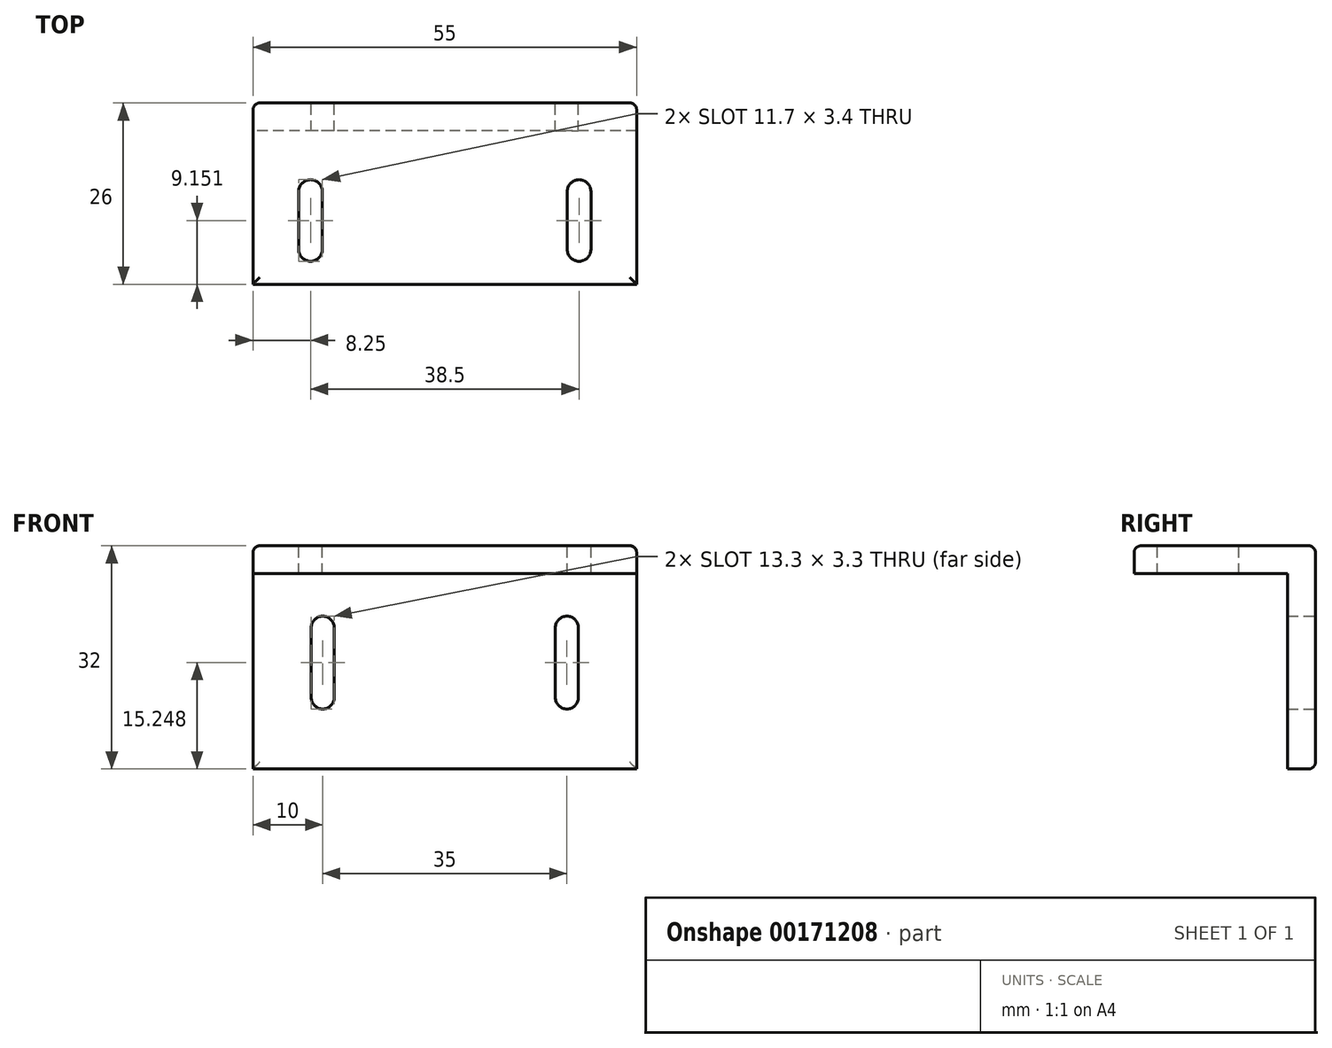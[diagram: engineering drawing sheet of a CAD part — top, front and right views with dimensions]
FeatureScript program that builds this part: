
annotation { "Feature Type Name" : "Feature", "Feature Type Description" : "" }
export const myFeature = defineFeature(function(context is Context, id is Id, definition is map)
    precondition{}
    {
        {
            var Q0;
            Q0=qCreatedBy(makeId("Right.planeOp"),FACE);
            var sketch = newSketch(context, id + "F0", { "sketchPlane" : qUnion([Q0])});
            skLineSegment(sketch, "E0.bottom", {"start": v(0, 0) * mm, "end": v(-26, 0) * mm});
            skLineSegment(sketch, "E0.top", {"start": v(0, -32) * mm, "end": v(-4, -32) * mm});
            skLineSegment(sketch, "E0.left", {"start": v(0, 0) * mm, "end": v(0, -32) * mm});
            skLineSegment(sketch, "E0.right", {"start": v(-26, 0) * mm, "end": v(-26, -4) * mm});
            skLineSegment(sketch, "E1.top", {"start": v(-26, -4) * mm, "end": v(-4, -4) * mm});
            skLineSegment(sketch, "E1.right", {"start": v(-4, -32) * mm, "end": v(-4, -4) * mm});
            skSolve(sketch);
        }
        {
            var Q0;
            Q0=makeQuery(id+"F0.imprint","IMPRINT",FACE,{"disambiguationData":[TD([[makeQuery(id+"F0.imprint","IMPRINT",EDGE,{"derivedFrom":sQuery(id+"F0.wireOp",EDGE,"E0.bottom")}),1.0]])]});
            extrude(context, id + "F1", {"entities" : qUnion([Q0]), "endBound" : BoundingType.SYMMETRIC, "depth" : 55 * mm});
        }
        {
            var Q0;
            Q0=qCreatedBy(makeId("Top.planeOp"),FACE);
            var sketch = newSketch(context, id + "F2", { "sketchPlane" : qUnion([Q0])});
            skArc(sketch, "E2", {"start": v(-20.95, -21) * mm, "mid": v(-19.25, -22.7) * mm, "end": v(-17.55, -21) * mm});
            skLineSegment(sketch, "E3.bottom", {"start": v(-17.55, -12.7) * mm, "end": v(-17.55, -12.7) * mm});
            skLineSegment(sketch, "E3.top", {"start": v(-19.25, -21) * mm, "end": v(-19.25, -21) * mm});
            skLineSegment(sketch, "E4.bottom", {"start": v(-20.95, -21) * mm, "end": v(-17.55, -21) * mm});
            skLineSegment(sketch, "E4.right", {"start": v(-17.55, -21) * mm, "end": v(-17.55, -12.7) * mm});
            skArc(sketch, "E5", {"start": v(-17.55, -12.7) * mm, "mid": v(-19.25, -11) * mm, "end": v(-20.95, -12.7) * mm});
            skLineSegment(sketch, "E6", {"start": v(-20.95, -21) * mm, "end": v(-20.95, -12.7) * mm});
            skLineSegment(sketch, "E7.MirrorCS", {"start": v(19.25, -21) * mm, "end": v(19.25, -21) * mm});
            skLineSegment(sketch, "E8.MirrorCS", {"start": v(20.95, -21) * mm, "end": v(17.55, -21) * mm});
            skArc(sketch, "E9.MirrorCS", {"start": v(17.55, -12.7) * mm, "mid": v(19.25, -11) * mm, "end": v(20.95, -12.7) * mm});
            skArc(sketch, "E10.MirrorCS", {"start": v(20.95, -21) * mm, "mid": v(19.25, -22.7) * mm, "end": v(17.55, -21) * mm});
            skLineSegment(sketch, "E11.MirrorCS", {"start": v(17.55, -12.7) * mm, "end": v(17.55, -12.7) * mm});
            skLineSegment(sketch, "E12.MirrorCS", {"start": v(20.95, -21) * mm, "end": v(20.95, -12.7) * mm});
            skLineSegment(sketch, "E13.MirrorCS", {"start": v(17.55, -21) * mm, "end": v(17.55, -12.7) * mm});
            skSolve(sketch);
        }
        {
            var Q0;
            Q0=qSketchRegion(id+"F2",true);
            extrude(context, id + "F3", {"entities" : qUnion([Q0]), "operationType" : NewBodyOperationType.REMOVE, "endBound" : BoundingType.THROUGH_ALL, "oppositeDirection" : true, "depth" : 10 * mm});
        }
        {
            var Q0;
            Q0=makeQuery(id+"F1.opExtrude","SWEPT_EDGE",EDGE,{"disambiguationData":[OSD([sQuery(id+"F0.wireOp",EDGE,"E0.top"),sQuery(id+"F0.wireOp",EDGE,"E0.left")])]});
            var Q1;
            Q1=makeQuery(id+"F1.opExtrude","CAP_EDGE",EDGE,{"disambiguationData":[OSD([sQuery(id+"F0.wireOp",EDGE,"E0.left")])],"isStart":true});
            var Q2;
            Q2=makeQuery(id+"F1.opExtrude","CAP_EDGE",EDGE,{"disambiguationData":[OSD([sQuery(id+"F0.wireOp",EDGE,"E0.left")])],"isStart":false});
            var Q3;
            Q3=makeQuery(id+"F1.opExtrude","SWEPT_EDGE",EDGE,{"disambiguationData":[OSD([sQuery(id+"F0.wireOp",EDGE,"E0.bottom"),sQuery(id+"F0.wireOp",EDGE,"E0.left")])]});
            var Q4;
            {var subQ0=sQuery(id+"F0.wireOp",EDGE,"E0.bottom");var subQ1=sQuery(id+"F0.wireOp",EDGE,"E0.right");Q4=makeQuery(id+"F3.boolean.opBoolean","SPLIT",EDGE,{"disambiguationData":[TD([makeQuery(id+"F3.opExtrude","SWEPT_FACE",FACE,{"disambiguationData":[OSD([sQuery(id+"F2.wireOp",EDGE,"orV0qqHB-hAtN-c7Y2-ubxL-00y3ppTQjBUW.left")])]})])],"derivedFrom":makeQuery(id+"F1.opExtrude","SWEPT_EDGE",EDGE,{"disambiguationData":[OSD([subQ0,subQ1])]})});}
            var Q5;
            {var subQ0=sQuery(id+"F0.wireOp",EDGE,"E0.bottom");var subQ1=sQuery(id+"F0.wireOp",EDGE,"E0.right");Q5=makeQuery(id+"F3.boolean.opBoolean","SPLIT",EDGE,{"disambiguationData":[TD([makeQuery(id+"F3.opExtrude","SWEPT_FACE",FACE,{"disambiguationData":[OSD([sQuery(id+"F2.wireOp",EDGE,"f2039e86-be7c-4192-a979-50250873df190.MirrorCS")])]})])],"derivedFrom":makeQuery(id+"F1.opExtrude","SWEPT_EDGE",EDGE,{"disambiguationData":[OSD([subQ0,subQ1])]})});}
            var Q6;
            Q6=makeQuery(id+"F1.opExtrude","CAP_EDGE",EDGE,{"disambiguationData":[OSD([sQuery(id+"F0.wireOp",EDGE,"E0.bottom")])],"isStart":true});
            var Q7;
            Q7=makeQuery(id+"F3.boolean.opBoolean","COPY",EDGE,{"derivedFrom":makeQuery(id+"F3.opExtrude","CAP_EDGE",EDGE,{"disambiguationData":[OSD([sQuery(id+"F2.wireOp",EDGE,"40ea4abb-f649-4232-bc7a-a4a23449ed800.MirrorCS")])],"isStart":true})});
            var Q8;
            Q8=makeQuery(id+"F1.opExtrude","CAP_EDGE",EDGE,{"disambiguationData":[OSD([sQuery(id+"F0.wireOp",EDGE,"E0.bottom")])],"isStart":false});
            var Q9;
            Q9=makeQuery(id+"F3.boolean.opBoolean","COPY",EDGE,{"derivedFrom":makeQuery(id+"F3.opExtrude","CAP_EDGE",EDGE,{"disambiguationData":[OSD([sQuery(id+"F2.wireOp",EDGE,"orV0qqHB-hAtN-c7Y2-ubxL-00y3ppTQjBUW.left")])],"isStart":true})});
            var Q10;
            Q10=makeQuery(id+"F3.boolean.opBoolean","COPY",EDGE,{"derivedFrom":makeQuery(id+"F3.opExtrude","CAP_EDGE",EDGE,{"disambiguationData":[OSD([sQuery(id+"F2.wireOp",EDGE,"f2039e86-be7c-4192-a979-50250873df190.MirrorCS")])],"isStart":true})});
            fillet(context, id + "F4", {"entities" : qUnion([Q0, Q1, Q2, Q3, Q4, Q5, Q6, Q7, Q8, Q9, Q10]), "radius" : 1 * mm, "tangentPropagation" : true, "allowEdgeOverflow" : false});
        }
        {
            var Q0;
            Q0=makeQuery(id+"F1.opExtrude","SWEPT_FACE",FACE,{"disambiguationData":[OSD([sQuery(id+"F0.wireOp",EDGE,"E0.left")])]});
            var sketch = newSketch(context, id + "F5", { "sketchPlane" : qUnion([Q0])});
            skArc(sketch, "E14", {"start": v(15.85, -21.75) * mm, "mid": v(17.5, -23.4) * mm, "end": v(19.15, -21.75) * mm});
            skArc(sketch, "E15", {"start": v(19.15, -11.75) * mm, "mid": v(17.5, -10.1) * mm, "end": v(15.85, -11.75) * mm});
            skLineSegment(sketch, "E16", {"start": v(15.85, -11.75) * mm, "end": v(15.85, -21.75) * mm});
            skLineSegment(sketch, "E17", {"start": v(19.15, -11.75) * mm, "end": v(19.15, -21.75) * mm});
            skArc(sketch, "E18.MirrorCS", {"start": v(-15.85, -21.75) * mm, "mid": v(-17.5, -23.4) * mm, "end": v(-19.15, -21.75) * mm});
            skArc(sketch, "E19.MirrorCS", {"start": v(-19.15, -11.75) * mm, "mid": v(-17.5, -10.1) * mm, "end": v(-15.85, -11.75) * mm});
            skLineSegment(sketch, "E20.MirrorCS", {"start": v(-15.85, -11.75) * mm, "end": v(-15.85, -21.75) * mm});
            skLineSegment(sketch, "E21.MirrorCS", {"start": v(-19.15, -11.75) * mm, "end": v(-19.15, -21.75) * mm});
            skSolve(sketch);
        }
        {
            var Q0;
            Q0=qSketchRegion(id+"F5",true);
            extrude(context, id + "F6", {"entities" : qUnion([Q0]), "operationType" : NewBodyOperationType.REMOVE, "endBound" : BoundingType.THROUGH_ALL, "oppositeDirection" : true, "depth" : 25 * mm});
        }
    });
